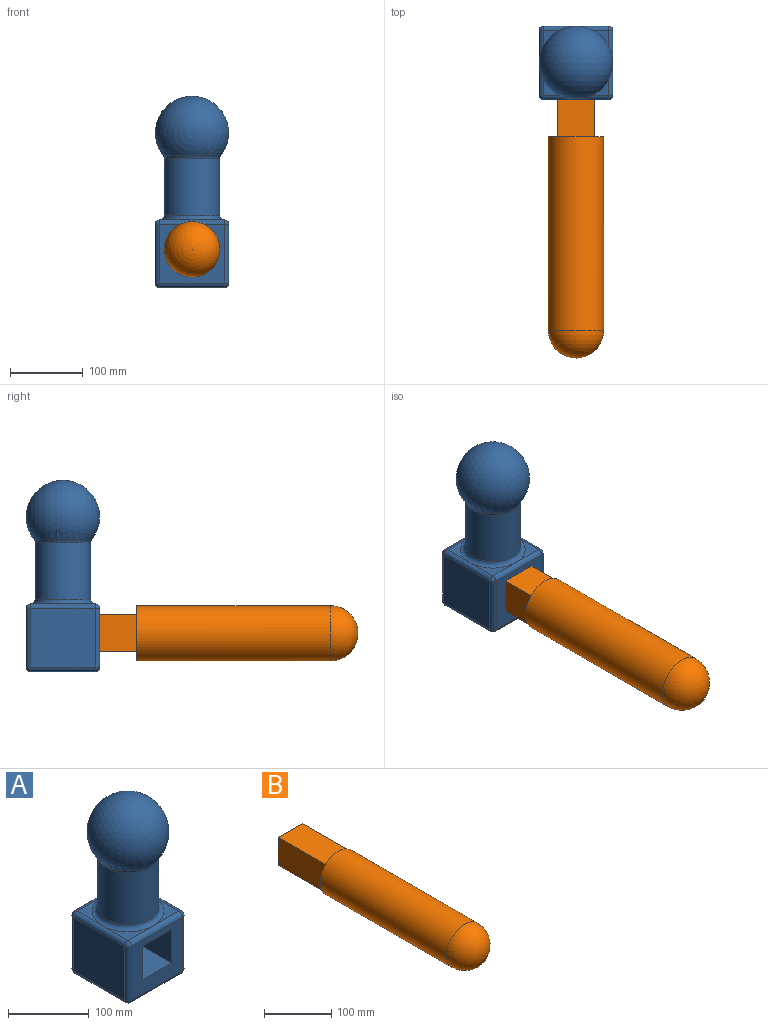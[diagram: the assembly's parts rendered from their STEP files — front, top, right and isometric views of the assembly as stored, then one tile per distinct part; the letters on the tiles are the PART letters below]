
ASSEMBLY  parts=2 mates=1
PART A: 38 faces, bbox 106x106x263.6 mm
  f0: plane 44.45x44.45mm, normal (0,0,1), area 424mm2, adj f17,f31,f32
  f1: plane 44.45x44.45mm, normal (0,0,1), area 424mm2, adj f17,f21,f31
  f2: plane 44.45x44.45mm, normal (0,0,1), area 424mm2, adj f17,f21,f22
  f3: cylinder r=38.1mm len=78.11mm, axis (0,0,-1), area 18698.7mm2, adj f16,f17
  f4: plane 88.9x80.52mm, normal (1,0,0), area 7158.1mm2, adj f26,f31,f34,f37
  f5: plane 88.9x80.52mm, normal (0,1,0), area 7158.1mm2, adj f23,f32,f33,f37
  f6: plane 88.9x80.52mm, normal (-1,0,0), area 7158.1mm2, adj f18,f22,f23,f24
  f7: plane 88.9x80.52mm, normal (0,-1,0), area 4577.4mm2, adj f11,f12,f13,f14,f18,f21,f25,f26
  f8: plane 44.45x44.45mm, normal (0,0,1), area 424mm2, adj f17,f22,f32
  f9: plane 88.9x88.9mm, normal (0,0,-1), area 7903.2mm2, adj f24,f25,f33,f34
  f10: sphere r=50.49mm, area 26002.2mm2, adj f16
  f11: plane 50.8x50.8mm, normal (-1,0,0), area 2580.6mm2, adj f7,f12,f14,f15
  f12: plane 50.8x50.8mm, normal (0,0,-1), area 2580.6mm2, adj f7,f11,f13,f15
  f13: plane 50.8x50.8mm, normal (1,0,0), area 2580.6mm2, adj f7,f12,f14,f15
  f14: plane 50.8x50.8mm, normal (0,0,1), area 2580.6mm2, adj f7,f11,f13,f15
  f15: plane 50.8x50.8mm, normal (0,-1,0), area 2580.6mm2, adj f11,f12,f13,f14
  f16: torus R=44.45mm, axis (0,0,1), area 1035.5mm2, adj f3,f10
  f17: torus R=44.45mm, axis (0,0,1), area 2532.4mm2, adj f0,f1,f2,f3,f8
  f18: cylinder r=6.35mm len=80.52mm, axis (0,0,-1), area 803.1mm2, adj f6,f7,f19,f20
  f19: sphere r=6.35mm, area 63.3mm2, adj f18,f21,f22
  f20: sphere r=6.35mm, area 63.3mm2, adj f18,f24,f25
  f21: cylinder r=6.35mm len=88.9mm, axis (-1,0,0), area 886.7mm2, adj f1,f2,f7,f19,f27
  f22: cylinder r=6.35mm len=88.9mm, axis (0,1,0), area 886.7mm2, adj f2,f6,f8,f19,f28
  f23: cylinder r=6.35mm len=80.52mm, axis (0,0,1), area 803.1mm2, adj f5,f6,f28,f29
  f24: cylinder r=6.35mm len=88.9mm, axis (0,-1,0), area 886.7mm2, adj f6,f9,f20,f29
  f25: cylinder r=6.35mm len=88.9mm, axis (1,0,0), area 886.7mm2, adj f7,f9,f20,f30
  f26: cylinder r=6.35mm len=80.52mm, axis (0,0,1), area 803.1mm2, adj f4,f7,f27,f30
  f27: sphere r=6.35mm, area 63.3mm2, adj f21,f26,f31
  f28: sphere r=6.35mm, area 63.3mm2, adj f22,f23,f32
  f29: sphere r=6.35mm, area 63.3mm2, adj f23,f24,f33
  f30: sphere r=6.35mm, area 63.3mm2, adj f25,f26,f34
  f31: cylinder r=6.35mm len=88.9mm, axis (0,-1,0), area 886.7mm2, adj f0,f1,f4,f27,f35
  f32: cylinder r=6.35mm len=88.9mm, axis (1,0,0), area 886.7mm2, adj f0,f5,f8,f28,f35
  f33: cylinder r=6.35mm len=88.9mm, axis (-1,0,0), area 886.7mm2, adj f5,f9,f29,f36
  f34: cylinder r=6.35mm len=88.9mm, axis (0,1,0), area 886.7mm2, adj f4,f9,f30,f36
  f35: sphere r=6.35mm, area 63.3mm2, adj f31,f32,f37
  f36: sphere r=6.35mm, area 63.3mm2, adj f33,f34,f37
  f37: cylinder r=6.35mm len=80.52mm, axis (0,0,-1), area 803.1mm2, adj f4,f5,f35,f36
PART B: 8 faces, bbox 76.2x406.4x76.2 mm
  f0: plane 101.6x50.8mm, normal (1,0,0), area 5161.3mm2, adj f1,f3,f4,f5
  f1: plane 101.6x50.8mm, normal (0,0,1), area 5161.3mm2, adj f0,f2,f4,f5
  f2: plane 101.6x50.8mm, normal (-1,0,0), area 5161.3mm2, adj f1,f3,f4,f5
  f3: plane 101.6x50.8mm, normal (0,0,-1), area 5161.3mm2, adj f0,f2,f4,f5
  f4: plane 50.8x50.8mm, normal (0,1,0), area 2580.6mm2, adj f0,f1,f2,f3
  f5: plane 76.2x76.2mm, normal (0,1,0), area 1979.7mm2, adj f0,f1,f2,f3,f6
  f6: cylinder r=38.1mm len=266.7mm, axis (0,1,0), area 63845.1mm2, adj f5,f7
  f7: sphere r=38.1mm, area 9120.7mm2, adj f6
PLACE A t=(-51.39,216.72,64.78)mm fixed
PLACE B t=(-51.39,216.72,117.52)mm
MATE fastened B.f6 <-> A.f15  axis (0,1,0) through (-51.39,216.72,117.52)mm
